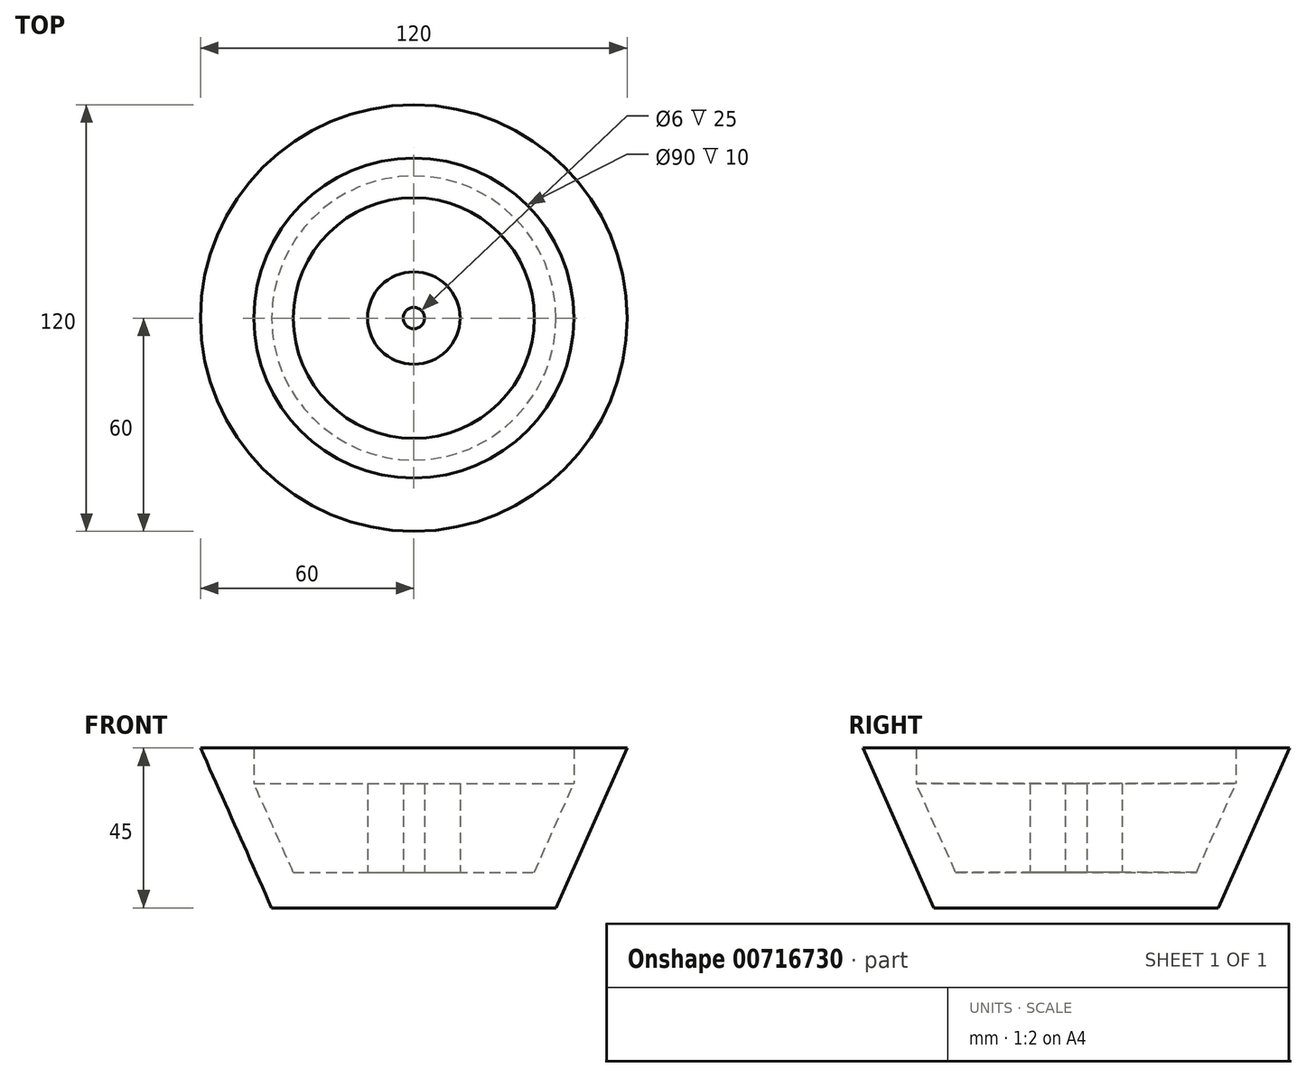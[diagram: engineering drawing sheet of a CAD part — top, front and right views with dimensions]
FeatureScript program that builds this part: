
annotation { "Feature Type Name" : "Feature", "Feature Type Description" : "" }
export const myFeature = defineFeature(function(context is Context, id is Id, definition is map)
    precondition{}
    {
        {
            var Q0;
            Q0=qCreatedBy(makeId("Front.planeOp"),FACE);
            var sketch = newSketch(context, id + "F0", { "sketchPlane" : qUnion([Q0])});
            skLineSegment(sketch, "E0", {"start": v(0, -129.45) * mm, "end": v(0, 136.53) * mm, "construction": true});
            skLineSegment(sketch, "E1", {"start": v(0, -35) * mm, "end": v(0, -45) * mm});
            skLineSegment(sketch, "E2", {"start": v(0, -45) * mm, "end": v(-40, -45) * mm});
            skLineSegment(sketch, "E3", {"start": v(-40, -45) * mm, "end": v(-60, 0) * mm});
            skLineSegment(sketch, "E4", {"start": v(-13, -10) * mm, "end": v(-3, -10) * mm});
            skLineSegment(sketch, "E5", {"start": v(-3, -10) * mm, "end": v(-3, -35) * mm});
            skLineSegment(sketch, "E6", {"start": v(-3, -35) * mm, "end": v(0, -35) * mm});
            skLineSegment(sketch, "E7", {"start": v(-13, -10) * mm, "end": v(-13, -35) * mm});
            skLineSegment(sketch, "E8", {"start": v(-13, -35) * mm, "end": v(-33.89, -35) * mm});
            skLineSegment(sketch, "E9", {"start": v(-45, 0) * mm, "end": v(-60, 0) * mm});
            skLineSegment(sketch, "E10", {"start": v(-45, 0) * mm, "end": v(-45, -10) * mm});
            skLineSegment(sketch, "E11", {"start": v(-45, -10) * mm, "end": v(-33.89, -35) * mm});
            skSolve(sketch);
        }
        {
            var Q0;
            Q0=makeQuery(id+"F0.imprint","IMPRINT",FACE,{"disambiguationData":[TD([[makeQuery(id+"F0.imprint","IMPRINT",EDGE,{"derivedFrom":sQuery(id+"F0.wireOp",EDGE,"E1")}),-1.0]])]});
            var Q1;
            Q1=sQuery(id+"F0.wireOp",EDGE,"E0");
            revolve(context, id + "F1", {"surfaceOperationType" : NewSurfaceOperationType.NEW, "entities" : qUnion([Q0]), "axis" : qUnion([Q1]), "revolveType" : RevolveType.FULL});
        }
    });
